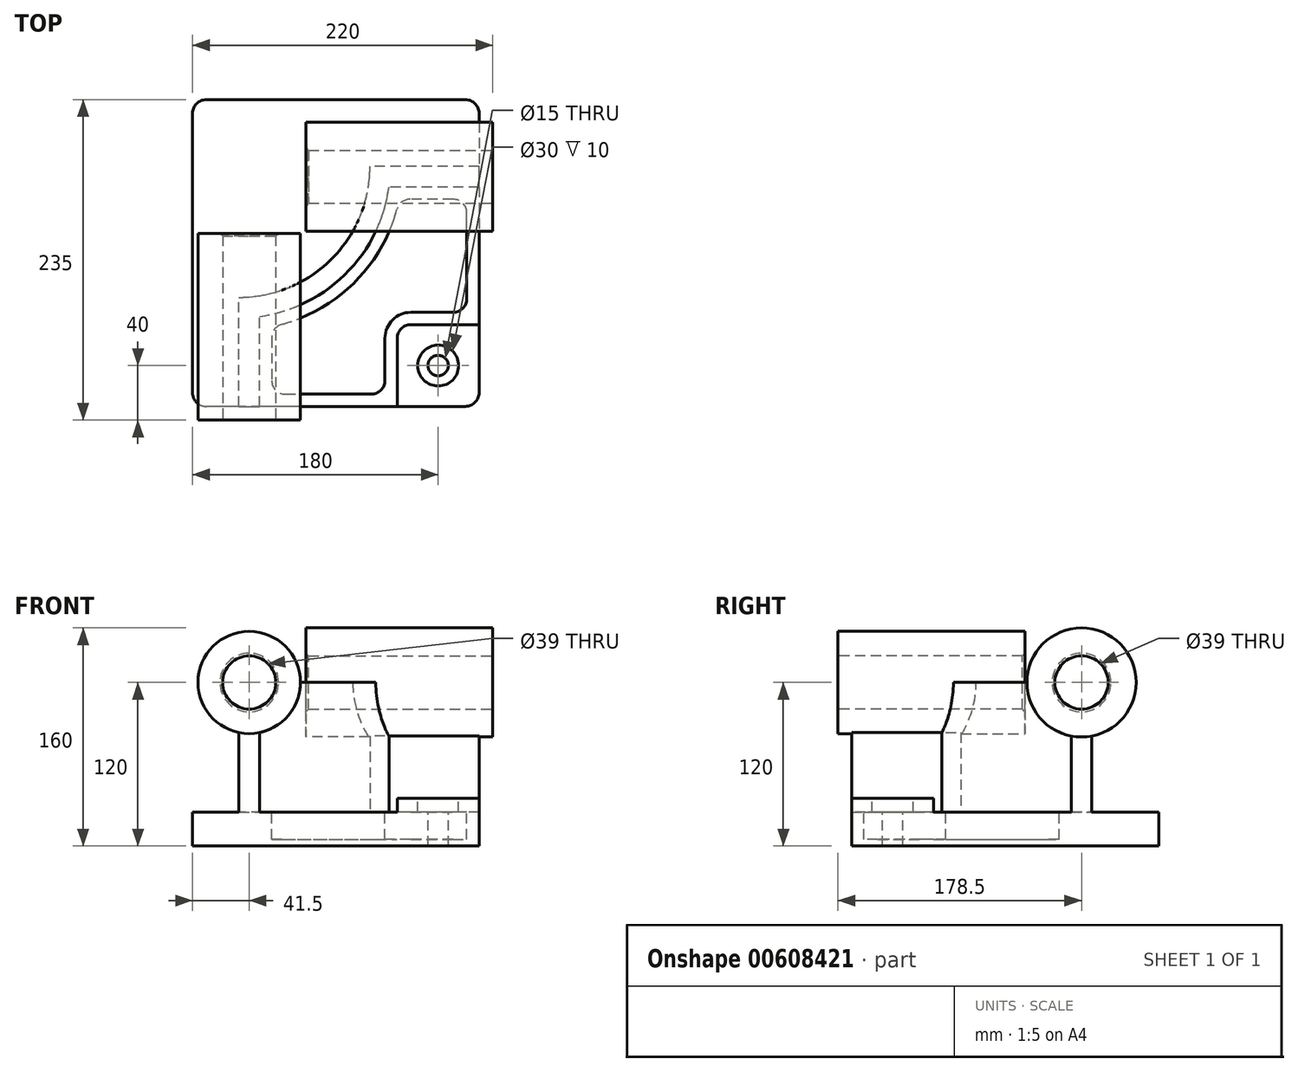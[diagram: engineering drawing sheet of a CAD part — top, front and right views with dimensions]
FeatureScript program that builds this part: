
annotation { "Feature Type Name" : "Feature", "Feature Type Description" : "" }
export const myFeature = defineFeature(function(context is Context, id is Id, definition is map)
    precondition{}
    {
        {
            var Q0;
            Q0=qCreatedBy(makeId("Top.planeOp"),FACE);
            var sketch = newSketch(context, id + "F0", { "sketchPlane" : qUnion([Q0])});
            skLineSegment(sketch, "E0.bottom", {"start": v(105, 112.5) * mm, "end": v(-105, 112.5) * mm});
            skLineSegment(sketch, "E0.top", {"start": v(105, -112.5) * mm, "end": v(-105, -112.5) * mm});
            skLineSegment(sketch, "E0.left", {"start": v(105, 112.5) * mm, "end": v(105, -112.5) * mm});
            skLineSegment(sketch, "E0.right", {"start": v(-105, 112.5) * mm, "end": v(-105, -112.5) * mm});
            skPoint(sketch, "E0.middle", {"position": v(0, 0) * mm});
            skSolve(sketch);
        }
        {
            var Q0;
            Q0=makeQuery(id+"F0.imprint","IMPRINT",FACE,{"disambiguationData":[TD([[makeQuery(id+"F0.imprint","IMPRINT",EDGE,{"derivedFrom":sQuery(id+"F0.wireOp",EDGE,"E0.bottom")}),1.0]])]});
            extrude(context, id + "F1", {"entities" : qUnion([Q0]), "depth" : 25 * mm, "offsetDistance" : 25 * mm});
        }
        {
            var Q0;
            Q0=makeQuery(id+"F1.opExtrude","CAP_FACE",FACE,{"disambiguationData":[OSD([sQuery(id+"F0.wireOp",EDGE,"E0.bottom"),sQuery(id+"F0.wireOp",EDGE,"E0.top"),sQuery(id+"F0.wireOp",EDGE,"E0.left"),sQuery(id+"F0.wireOp",EDGE,"E0.right")])],"isStart":false});
            var sketch = newSketch(context, id + "F2", { "sketchPlane" : qUnion([Q0])});
            skLineSegment(sketch, "E1", {"start": v(-71, -112.5) * mm, "end": v(-71, -32.5) * mm});
            skLineSegment(sketch, "E2", {"start": v(105, 63.5) * mm, "end": v(25, 63.5) * mm});
            skArc(sketch, "E3", {"start": v(-71, -32.5) * mm, "mid": v(-3.12, -4.38) * mm, "end": v(25, 63.5) * mm});
            skLineSegment(sketch, "E4", {"start": v(-71, 63.5) * mm, "end": v(25, 63.5) * mm, "construction": true});
            skLineSegment(sketch, "E5", {"start": v(-71, -32.5) * mm, "end": v(-71, 63.5) * mm, "construction": true});
            skLineSegment(sketch, "E6.0", {"start": v(105, 48.5) * mm, "end": v(38.98, 48.5) * mm});
            skArc(sketch, "E6.1", {"start": v(-56, -46.48) * mm, "mid": v(7.49, -14.99) * mm, "end": v(38.98, 48.5) * mm});
            skLineSegment(sketch, "E6.2", {"start": v(-56, -112.5) * mm, "end": v(-56, -46.48) * mm});
            skSolve(sketch);
        }
        {
            var Q0;
            {var subQ3=sQuery(id+"F2.wireOp",EDGE,"E1");Q0=makeQuery(id+"F2.imprint","IMPRINT",FACE,{"disambiguationData":[TD([[makeQuery(id+"F2.imprint","IMPRINT",EDGE,{"derivedFrom":subQ3}),-1.0]])]});}
            extrude(context, id + "F3", {"entities" : qUnion([Q0]), "operationType" : NewBodyOperationType.ADD, "depth" : 95 * mm, "offsetDistance" : 25 * mm});
        }
        {
            var Q0;
            {var subQ0=sQuery(id+"F0.wireOp",EDGE,"E0.top");Q0=makeQuery(id+"F3.boolean.opBoolean","MERGE",FACE,{"derivedFrom":[makeQuery(id+"F1.opExtrude","SWEPT_FACE",FACE,{"disambiguationData":[OSD([subQ0])]}),makeQuery(id+"F3.opExtrude","SWEPT_FACE",FACE,{"disambiguationData":[OSD([subQ0])]})]});}
            var sketch = newSketch(context, id + "F4", { "sketchPlane" : qUnion([Q0])});
            skCircle(sketch, "E7", {"center": v(-63.5, 120) * mm, "radius": 37.5 * mm});
            skSolve(sketch);
        }
        {
            var Q0;
            Q0 = qSketchRegion(id + "F4", true);
            extrude(context, id + "F5", {"entities" : qUnion([Q0]), "operationType" : NewBodyOperationType.ADD, "depth" : 10 * mm, "offsetDistance" : 25 * mm, "hasSecondDirection" : true, "secondDirectionOppositeDirection" : true, "secondDirectionDepth" : 127 * mm});
        }
        {
            var Q0;
            {var subQ0=sQuery(id+"F0.wireOp",EDGE,"E0.left");Q0=makeQuery(id+"F3.boolean.opBoolean","MERGE",FACE,{"derivedFrom":[makeQuery(id+"F1.opExtrude","SWEPT_FACE",FACE,{"disambiguationData":[OSD([subQ0])]}),makeQuery(id+"F3.opExtrude","SWEPT_FACE",FACE,{"disambiguationData":[OSD([subQ0])]})]});}
            var sketch = newSketch(context, id + "F6", { "sketchPlane" : qUnion([Q0])});
            skCircle(sketch, "E8", {"center": v(56, 120) * mm, "radius": 40 * mm});
            skSolve(sketch);
        }
        {
            var Q0;
            Q0 = qSketchRegion(id + "F6", true);
            extrude(context, id + "F7", {"entities" : qUnion([Q0]), "operationType" : NewBodyOperationType.ADD, "depth" : 10 * mm, "offsetDistance" : 25 * mm, "hasSecondDirection" : true, "secondDirectionOppositeDirection" : true, "secondDirectionDepth" : 127 * mm});
        }
        {
            var Q0;
            {var subQ0=sQuery(id+"F0.wireOp",EDGE,"E0.left");var subQ1=sQuery(id+"F0.wireOp",EDGE,"E0.top");Q0=makeQuery(id+"F3.boolean.opBoolean","SPLIT",FACE,{"disambiguationData":[TD([makeQuery(id+"F3.opExtrude","SWEPT_FACE",FACE,{"disambiguationData":[OSD([sQuery(id+"F2.wireOp",EDGE,"E6.0")])]})])],"derivedFrom":makeQuery(id+"F1.opExtrude","CAP_FACE",FACE,{"disambiguationData":[OSD([sQuery(id+"F0.wireOp",EDGE,"E0.bottom"),subQ1,subQ0,sQuery(id+"F0.wireOp",EDGE,"E0.right")])],"isStart":false})});}
            var sketch = newSketch(context, id + "F8", { "sketchPlane" : qUnion([Q0])});
            skLineSegment(sketch, "E9.bottom", {"start": v(105, -112.5) * mm, "end": v(45, -112.5) * mm});
            skLineSegment(sketch, "E9.top", {"start": v(105, -52.5) * mm, "end": v(45, -52.5) * mm});
            skLineSegment(sketch, "E9.left", {"start": v(105, -112.5) * mm, "end": v(105, -52.5) * mm});
            skLineSegment(sketch, "E9.right", {"start": v(45, -112.5) * mm, "end": v(45, -52.5) * mm});
            skSolve(sketch);
        }
        {
            var Q0;
            Q0=makeQuery(id+"F8.imprint","IMPRINT",FACE,{"disambiguationData":[TD([[makeQuery(id+"F8.imprint","IMPRINT",EDGE,{"derivedFrom":sQuery(id+"F8.wireOp",EDGE,"E9.bottom")}),-1.0]])]});
            extrude(context, id + "F9", {"entities" : qUnion([Q0]), "operationType" : NewBodyOperationType.ADD, "depth" : 10 * mm, "offsetDistance" : 25 * mm});
        }
        {
            var Q0;
            Q0=makeQuery(id+"F9.opExtrude","SWEPT_EDGE",EDGE,{"disambiguationData":[OSD([sQuery(id+"F8.wireOp",EDGE,"E9.top"),sQuery(id+"F8.wireOp",EDGE,"E9.right")])]});
            fillet(context, id + "F10", {"entities" : qUnion([Q0]), "radius" : 10 * mm, "tangentPropagation" : true, "allowEdgeOverflow" : false});
        }
        {
            var Q0;
            {var subQ0=sQuery(id+"F0.wireOp",EDGE,"E0.left");var subQ1=sQuery(id+"F0.wireOp",EDGE,"E0.top");Q0=makeQuery(id+"F3.boolean.opBoolean","SPLIT",FACE,{"disambiguationData":[TD([makeQuery(id+"F3.opExtrude","SWEPT_FACE",FACE,{"disambiguationData":[OSD([sQuery(id+"F2.wireOp",EDGE,"E6.0")])]})])],"derivedFrom":makeQuery(id+"F1.opExtrude","CAP_FACE",FACE,{"disambiguationData":[OSD([sQuery(id+"F0.wireOp",EDGE,"E0.bottom"),subQ1,subQ0,sQuery(id+"F0.wireOp",EDGE,"E0.right")])],"isStart":false})});}
            var sketch = newSketch(context, id + "F11", { "sketchPlane" : qUnion([Q0])});
            skLineSegment(sketch, "E10.0", {"start": v(-47, -54.08) * mm, "end": v(-47, -103.5) * mm});
            skArc(sketch, "E10.1", {"start": v(46.58, 39.5) * mm, "mid": v(13.85, -21.35) * mm, "end": v(-47, -54.08) * mm});
            skLineSegment(sketch, "E10.2", {"start": v(-47, -103.5) * mm, "end": v(36, -103.5) * mm});
            skLineSegment(sketch, "E10.3", {"start": v(96, 39.5) * mm, "end": v(46.58, 39.5) * mm});
            skLineSegment(sketch, "E10.4", {"start": v(36, -103.5) * mm, "end": v(36, -62.5) * mm});
            skArc(sketch, "E10.5", {"start": v(36, -62.5) * mm, "mid": v(41.56, -49.06) * mm, "end": v(55, -43.5) * mm});
            skLineSegment(sketch, "E10.6", {"start": v(55, -43.5) * mm, "end": v(96, -43.5) * mm});
            skLineSegment(sketch, "E10.7", {"start": v(96, -43.5) * mm, "end": v(96, 39.5) * mm});
            skSolve(sketch);
        }
        {
            var Q0;
            Q0=makeQuery(id+"F11.imprint","IMPRINT",FACE,{"disambiguationData":[TD([[makeQuery(id+"F11.imprint","IMPRINT",EDGE,{"derivedFrom":sQuery(id+"F11.wireOp",EDGE,"E10.0")}),1.0]])]});
            extrude(context, id + "F12", {"entities" : qUnion([Q0]), "operationType" : NewBodyOperationType.REMOVE, "oppositeDirection" : true, "depth" : 20 * mm, "offsetDistance" : 25 * mm});
        }
        {
            var Q0;
            Q0=makeQuery(id+"F9.opExtrude","CAP_FACE",FACE,{"disambiguationData":[OSD([sQuery(id+"F8.wireOp",EDGE,"E9.bottom"),sQuery(id+"F8.wireOp",EDGE,"E9.top"),sQuery(id+"F8.wireOp",EDGE,"E9.left"),sQuery(id+"F8.wireOp",EDGE,"E9.right")])],"isStart":false});
            var sketch = newSketch(context, id + "F13", { "sketchPlane" : qUnion([Q0])});
            skCircle(sketch, "E11", {"center": v(75, -82.5) * mm, "radius": 15 * mm});
            skSolve(sketch);
        }
        {
            var Q0;
            Q0=sQuery(id+"F13.wireOp",VERTEX,"E11.center");
            var Q1;
            Q1=makeQuery(id+"F1.opExtrude","SWEPT_BODY",BODY,{"disambiguationData":[OSD([sQuery(id+"F0.wireOp",EDGE,"E0.bottom"),sQuery(id+"F0.wireOp",EDGE,"E0.top"),sQuery(id+"F0.wireOp",EDGE,"E0.left"),sQuery(id+"F0.wireOp",EDGE,"E0.right")])]});
            hole(context, id + "F14", {"style" : HoleStyle.C_BORE, "endStyle" : HoleEndStyle.THROUGH, "holeDiameter" : 15 * mm, "cBoreDiameter" : 30 * mm, "cBoreDepth" : 10 * mm, "majorDiameter" : 5 * mm, "isTappedThrough" : true, "tappedDepth" : 12 * mm, "tapClearance" : 3, "locations" : qUnion([Q0]), "scope" : qUnion([Q1])});
        }
        {
            var Q0;
            Q0=makeQuery(id+"F12.boolean.opBoolean","COPY",EDGE,{"derivedFrom":makeQuery(id+"F12.opExtrude","SWEPT_EDGE",EDGE,{"disambiguationData":[OSD([sQuery(id+"F11.wireOp",EDGE,"E10.0"),sQuery(id+"F11.wireOp",EDGE,"E10.1")])]})});
            var Q1;
            Q1=makeQuery(id+"F12.boolean.opBoolean","COPY",EDGE,{"derivedFrom":makeQuery(id+"F12.opExtrude","SWEPT_EDGE",EDGE,{"disambiguationData":[OSD([sQuery(id+"F11.wireOp",EDGE,"E10.1"),sQuery(id+"F11.wireOp",EDGE,"E10.3")])]})});
            var Q2;
            Q2=makeQuery(id+"F12.boolean.opBoolean","COPY",EDGE,{"derivedFrom":makeQuery(id+"F12.opExtrude","SWEPT_EDGE",EDGE,{"disambiguationData":[OSD([sQuery(id+"F11.wireOp",EDGE,"E10.3"),sQuery(id+"F11.wireOp",EDGE,"E10.7")])]})});
            var Q3;
            Q3=makeQuery(id+"F12.boolean.opBoolean","COPY",EDGE,{"derivedFrom":makeQuery(id+"F12.opExtrude","SWEPT_EDGE",EDGE,{"disambiguationData":[OSD([sQuery(id+"F11.wireOp",EDGE,"E10.0"),sQuery(id+"F11.wireOp",EDGE,"E10.2")])]})});
            var Q4;
            Q4=makeQuery(id+"F12.boolean.opBoolean","COPY",EDGE,{"derivedFrom":makeQuery(id+"F12.opExtrude","SWEPT_EDGE",EDGE,{"disambiguationData":[OSD([sQuery(id+"F11.wireOp",EDGE,"E10.2"),sQuery(id+"F11.wireOp",EDGE,"E10.4")])]})});
            var Q5;
            Q5=makeQuery(id+"F12.boolean.opBoolean","COPY",EDGE,{"derivedFrom":makeQuery(id+"F12.opExtrude","SWEPT_EDGE",EDGE,{"disambiguationData":[OSD([sQuery(id+"F11.wireOp",EDGE,"E10.6"),sQuery(id+"F11.wireOp",EDGE,"E10.7")])]})});
            fillet(context, id + "F15", {"entities" : qUnion([Q0, Q1, Q2, Q3, Q4, Q5]), "radius" : 10 * mm, "tangentPropagation" : true, "allowEdgeOverflow" : false});
        }
        {
            var Q0;
            Q0=makeQuery(id+"F5.opExtrude","CAP_FACE",FACE,{"disambiguationData":[OSD([sQuery(id+"F4.wireOp",EDGE,"E7")])],"isStart":false});
            var sketch = newSketch(context, id + "F16", { "sketchPlane" : qUnion([Q0])});
            skCircle(sketch, "E12", {"center": v(-63.5, 120) * mm, "radius": 19.5 * mm});
            skSolve(sketch);
        }
        {
            var Q0;
            Q0 = qSketchRegion(id + "F16", true);
            extrude(context, id + "F17", {"entities" : qUnion([Q0]), "operationType" : NewBodyOperationType.REMOVE, "endBound" : BoundingType.THROUGH_ALL, "oppositeDirection" : true, "depth" : 25 * mm, "offsetDistance" : 25 * mm});
        }
        {
            var Q0;
            Q0=makeQuery(id+"F7.opExtrude","CAP_FACE",FACE,{"disambiguationData":[OSD([sQuery(id+"F6.wireOp",EDGE,"E8")])],"isStart":false});
            var sketch = newSketch(context, id + "F18", { "sketchPlane" : qUnion([Q0])});
            skCircle(sketch, "E13", {"center": v(56, 120) * mm, "radius": 19.5 * mm});
            skSolve(sketch);
        }
        {
            var Q0;
            Q0 = qSketchRegion(id + "F18", true);
            extrude(context, id + "F19", {"entities" : qUnion([Q0]), "operationType" : NewBodyOperationType.REMOVE, "endBound" : BoundingType.THROUGH_ALL, "oppositeDirection" : true, "depth" : 25 * mm, "offsetDistance" : 25 * mm});
        }
        {
            var Q0;
            Q0=makeQuery(id+"F17.boolean.opBoolean","COPY",EDGE,{"derivedFrom":makeQuery(id+"F17.opExtrude","CAP_EDGE",EDGE,{"disambiguationData":[OSD([sQuery(id+"F16.wireOp",EDGE,"E12")])],"isStart":true})});
            var Q1;
            Q1=makeQuery(id+"F19.boolean.opBoolean","COPY",EDGE,{"derivedFrom":makeQuery(id+"F19.opExtrude","CAP_EDGE",EDGE,{"disambiguationData":[OSD([sQuery(id+"F18.wireOp",EDGE,"E13")])],"isStart":true})});
            var Q2;
            Q2=makeQuery(id+"F19.boolean.opBoolean","INTERSECT",EDGE,{"derivedFrom":[makeQuery(id+"F7.opExtrude","CAP_FACE",FACE,{"disambiguationData":[OSD([sQuery(id+"F6.wireOp",EDGE,"E8")])],"isStart":true}),makeQuery(id+"F19.opExtrude","SWEPT_FACE",FACE,{"disambiguationData":[OSD([sQuery(id+"F18.wireOp",EDGE,"E13")])]})]});
            var Q3;
            Q3=makeQuery(id+"F17.boolean.opBoolean","INTERSECT",EDGE,{"derivedFrom":[makeQuery(id+"F5.opExtrude","CAP_FACE",FACE,{"disambiguationData":[OSD([sQuery(id+"F4.wireOp",EDGE,"E7")])],"isStart":true}),makeQuery(id+"F17.opExtrude","SWEPT_FACE",FACE,{"disambiguationData":[OSD([sQuery(id+"F16.wireOp",EDGE,"E12")])]})]});
            chamfer(context, id + "F20", {"entities" : qUnion([Q0, Q1, Q2, Q3]), "width" : 2 * mm, "tangentPropagation" : true});
        }
        {
            var Q0;
            Q0=makeQuery(id+"F1.opExtrude","SWEPT_EDGE",EDGE,{"disambiguationData":[OSD([sQuery(id+"F0.wireOp",EDGE,"E0.top"),sQuery(id+"F0.wireOp",EDGE,"E0.right")])]});
            var Q1;
            Q1=makeQuery(id+"F9.boolean.opBoolean","MERGE",EDGE,{"derivedFrom":[makeQuery(id+"F1.opExtrude","SWEPT_EDGE",EDGE,{"disambiguationData":[OSD([sQuery(id+"F0.wireOp",EDGE,"E0.top"),sQuery(id+"F0.wireOp",EDGE,"E0.left")])]}),makeQuery(id+"F9.opExtrude","SWEPT_EDGE",EDGE,{"disambiguationData":[OSD([sQuery(id+"F8.wireOp",EDGE,"E9.bottom"),sQuery(id+"F8.wireOp",EDGE,"E9.left")])]})]});
            var Q2;
            Q2=makeQuery(id+"F1.opExtrude","SWEPT_EDGE",EDGE,{"disambiguationData":[OSD([sQuery(id+"F0.wireOp",EDGE,"E0.bottom"),sQuery(id+"F0.wireOp",EDGE,"E0.left")])]});
            var Q3;
            Q3=makeQuery(id+"F1.opExtrude","SWEPT_EDGE",EDGE,{"disambiguationData":[OSD([sQuery(id+"F0.wireOp",EDGE,"E0.bottom"),sQuery(id+"F0.wireOp",EDGE,"E0.right")])]});
            fillet(context, id + "F21", {"entities" : qUnion([Q0, Q1, Q2, Q3]), "radius" : 10 * mm, "tangentPropagation" : true, "allowEdgeOverflow" : false});
        }
    });
